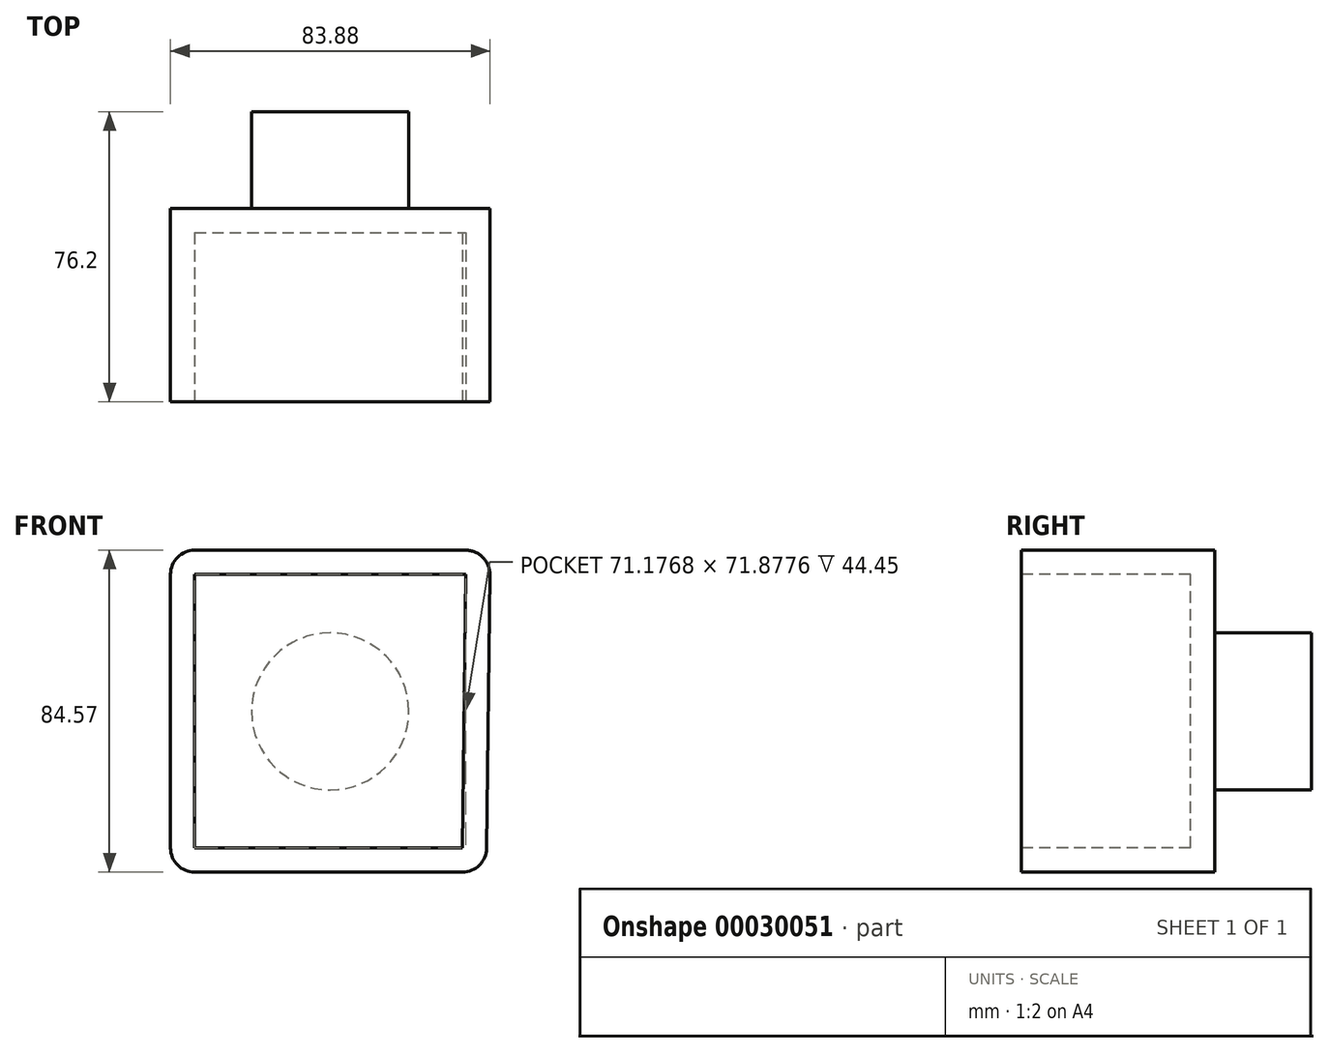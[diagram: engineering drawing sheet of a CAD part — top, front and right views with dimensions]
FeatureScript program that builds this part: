
annotation { "Feature Type Name" : "Feature", "Feature Type Description" : "" }
export const myFeature = defineFeature(function(context is Context, id is Id, definition is map)
    precondition{}
    {
        {
            var Q0;
            Q0=qCreatedBy(makeId("Front.planeOp"),FACE);
            var sketch = newSketch(context, id + "F0", { "sketchPlane" : qUnion([Q0])});
            skLineSegment(sketch, "E0", {"start": v(-46.4, -36.72) * mm, "end": v(-46.4, 47.85) * mm});
            skLineSegment(sketch, "E1", {"start": v(-46.4, 47.85) * mm, "end": v(37.55, 47.85) * mm});
            skLineSegment(sketch, "E2", {"start": v(-46.4, -36.72) * mm, "end": v(36.55, -36.72) * mm});
            skLineSegment(sketch, "E3", {"start": v(36.55, -36.72) * mm, "end": v(37.55, 47.85) * mm});
            skSolve(sketch);
        }
        {
            var Q0;
            Q0=makeQuery(id+"F0.imprint","IMPRINT",FACE,{"disambiguationData":[TD([[makeQuery(id+"F0.imprint","IMPRINT",EDGE,{"derivedFrom":sQuery(id+"F0.wireOp",EDGE,"E0")}),-1.0]])]});
            extrude(context, id + "F1", {"entities" : qUnion([Q0]), "oppositeDirection" : true, "depth" : 50.8 * mm});
        }
        {
            var Q0;
            Q0=makeQuery(id+"F1.opExtrude","CAP_FACE",FACE,{"disambiguationData":[OSD([sQuery(id+"F0.wireOp",EDGE,"E0"),sQuery(id+"F0.wireOp",EDGE,"E1"),sQuery(id+"F0.wireOp",EDGE,"E2"),sQuery(id+"F0.wireOp",EDGE,"E3")])],"isStart":true});
            shell(context, id + "F2", {"entities" : qUnion([Q0]), "thickness" : 6.35 * mm});
        }
        {
            var Q0;
            Q0=makeQuery(id+"F1.opExtrude","SWEPT_EDGE",EDGE,{"disambiguationData":[OSD([sQuery(id+"F0.wireOp",EDGE,"E1"),sQuery(id+"F0.wireOp",EDGE,"E3")])]});
            var Q1;
            Q1=makeQuery(id+"F1.opExtrude","SWEPT_EDGE",EDGE,{"disambiguationData":[OSD([sQuery(id+"F0.wireOp",EDGE,"E0"),sQuery(id+"F0.wireOp",EDGE,"E1")])]});
            var Q2;
            Q2=makeQuery(id+"F1.opExtrude","SWEPT_EDGE",EDGE,{"disambiguationData":[OSD([sQuery(id+"F0.wireOp",EDGE,"E2"),sQuery(id+"F0.wireOp",EDGE,"E3")])]});
            var Q3;
            Q3=makeQuery(id+"F1.opExtrude","SWEPT_EDGE",EDGE,{"disambiguationData":[OSD([sQuery(id+"F0.wireOp",EDGE,"E0"),sQuery(id+"F0.wireOp",EDGE,"E2")])]});
            fillet(context, id + "F3", {"entities" : qUnion([Q0, Q1, Q2, Q3]), "radius" : 6.35 * mm, "tangentPropagation" : true, "allowEdgeOverflow" : false});
        }
        {
            var Q0;
            Q0=makeQuery(id+"F1.opExtrude","CAP_FACE",FACE,{"disambiguationData":[OSD([sQuery(id+"F0.wireOp",EDGE,"E0"),sQuery(id+"F0.wireOp",EDGE,"E1"),sQuery(id+"F0.wireOp",EDGE,"E2"),sQuery(id+"F0.wireOp",EDGE,"E3")])],"isStart":false});
            var sketch = newSketch(context, id + "F4", { "sketchPlane" : qUnion([Q0])});
            skCircle(sketch, "E4", {"center": v(4.46, 5.49) * mm, "radius": 20.64 * mm});
            skSolve(sketch);
        }
        {
            var Q0;
            Q0=makeQuery(id+"F4.imprint","IMPRINT",FACE,{"disambiguationData":[TD([[makeQuery(id+"F4.imprint","IMPRINT",EDGE,{"derivedFrom":sQuery(id+"F4.wireOp",EDGE,"E4")}),1.0]])]});
            extrude(context, id + "F5", {"entities" : qUnion([Q0]), "operationType" : NewBodyOperationType.ADD, "depth" : 25.4 * mm});
        }
    });
